# Revit family: FU_Table_Sandler_Plania_PL50224
name_source: partatom
category: Furniture
units: mm (PartAtom-declared; Revit-internal decimal feet)

## family parameters
Always vertical = Yes
Cut with Voids When Loaded = No
OmniClass Number = 23.40.20.00
OmniClass Title = General Furniture and Specialties
Room Calculation Point = No
Shared = No
Work Plane-Based = No

## types (2) — shared parameters
Depth = 1200 mm
Description = 120cm x 240cm / 48″ x 95″ Rectangular oval table top with standard epoxy painted structural frame.
Frame = M1_B00 - Black
Height = 65 mm
Manufacturer = Sandler
URL = https://www.sandlerseating.com
Width = 2400 mm
zero-valued in all types: Default Elevation

## per-type parameters (varying)
| type | Top Finish | Top Type |
| PL50224 - Lacquered/Laminate | Wood - Solid Walnut | PL50224-Wood |
| PL50224 - HPL/Fenix | HPL - Solid - Black | PL50224-HPL : PL50224 - HPL |

note: column(s) folded — value = type name in every type: Model

## geometry (parser evidence)
native form markers: Sweep x6
no freeform markers — native parametric forms only
